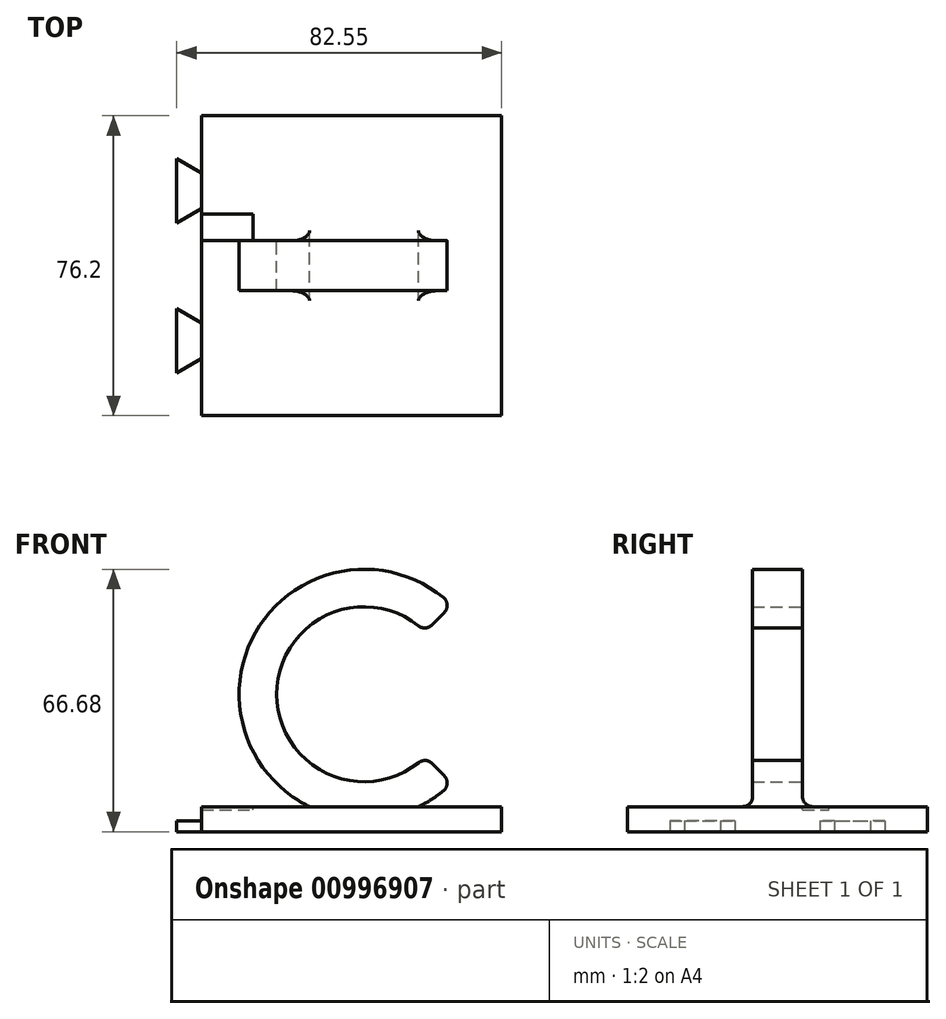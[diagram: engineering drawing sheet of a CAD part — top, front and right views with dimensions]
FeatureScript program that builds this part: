
annotation { "Feature Type Name" : "Feature", "Feature Type Description" : "" }
export const myFeature = defineFeature(function(context is Context, id is Id, definition is map)
    precondition{}
    {
        {
            var Q0;
            Q0=qCreatedBy(makeId("Top.planeOp"),FACE);
            var sketch = newSketch(context, id + "F0", { "sketchPlane" : qUnion([Q0])});
            skLineSegment(sketch, "E0.bottom", {"start": v(38.1, -38.1) * mm, "end": v(-38.1, -38.1) * mm});
            skLineSegment(sketch, "E0.top", {"start": v(38.1, 38.1) * mm, "end": v(-38.1, 38.1) * mm});
            skLineSegment(sketch, "E0.left", {"start": v(38.1, -38.1) * mm, "end": v(38.1, 38.1) * mm});
            skLineSegment(sketch, "E0.right", {"start": v(-38.1, -38.1) * mm, "end": v(-38.1, 38.1) * mm});
            skPoint(sketch, "E0.middle", {"position": v(0, 0) * mm});
            skSolve(sketch);
        }
        {
            var Q0;
            Q0=qCreatedBy(makeId("Front.planeOp"),FACE);
            var sketch = newSketch(context, id + "F1", { "sketchPlane" : qUnion([Q0])});
            skArc(sketch, "E1", {"start": v(25.4, 51.25) * mm, "mid": v(-28.58, 28.58) * mm, "end": v(25.4, 5.9) * mm});
            skLineSegment(sketch, "E2", {"start": v(16.41, 60.33) * mm, "end": v(-26.64, 60.33) * mm, "construction": true});
            skLineSegment(sketch, "E3", {"start": v(-19.56, -3.18) * mm, "end": v(26.32, -3.17) * mm, "construction": true});
            skArc(sketch, "E4", {"start": v(18.73, 44.45) * mm, "mid": v(-19.05, 28.58) * mm, "end": v(18.73, 12.7) * mm});
            skLineSegment(sketch, "E5", {"start": v(25.4, 51.25) * mm, "end": v(18.73, 44.45) * mm});
            skLineSegment(sketch, "E6", {"start": v(18.73, 12.7) * mm, "end": v(25.4, 5.9) * mm});
            skLineSegment(sketch, "E7", {"start": v(18.73, 44.45) * mm, "end": v(34.7, 28.8) * mm, "construction": true});
            skSolve(sketch);
        }
        {
            var Q0;
            Q0=qSketchRegion(id+"F0",true);
            extrude(context, id + "F2", {"entities" : qUnion([Q0]), "oppositeDirection" : true, "depth" : 6.35 * mm, "offsetDistance" : 25.4 * mm});
        }
        {
            var Q0;
            Q0=qSketchRegion(id+"F1",true);
            extrude(context, id + "F3", {"entities" : qUnion([Q0]), "operationType" : NewBodyOperationType.ADD, "endBound" : BoundingType.SYMMETRIC, "depth" : 12.7 * mm, "offsetDistance" : 25.4 * mm});
        }
        {
            var Q0;
            Q0=makeQuery(id+"F3.opExtrude","SWEPT_EDGE",EDGE,{"disambiguationData":[OSD([sQuery(id+"F1.wireOp",EDGE,"E1"),sQuery(id+"F1.wireOp",EDGE,"E5")])]});
            var Q1;
            Q1=makeQuery(id+"F3.opExtrude","SWEPT_EDGE",EDGE,{"disambiguationData":[OSD([sQuery(id+"F1.wireOp",EDGE,"E4"),sQuery(id+"F1.wireOp",EDGE,"E5")])]});
            var Q2;
            Q2=makeQuery(id+"F3.opExtrude","SWEPT_EDGE",EDGE,{"disambiguationData":[OSD([sQuery(id+"F1.wireOp",EDGE,"E4"),sQuery(id+"F1.wireOp",EDGE,"E6")])]});
            var Q3;
            Q3=makeQuery(id+"F3.opExtrude","SWEPT_EDGE",EDGE,{"disambiguationData":[OSD([sQuery(id+"F1.wireOp",EDGE,"E1"),sQuery(id+"F1.wireOp",EDGE,"E6")])]});
            var Q4;
            Q4=makeQuery(id+"F3.boolean.opBoolean","INTERSECT",EDGE,{"derivedFrom":[makeQuery(id+"F2.opExtrude","CAP_FACE",FACE,{"disambiguationData":[OSD([sQuery(id+"F0.wireOp",EDGE,"E0.bottom"),sQuery(id+"F0.wireOp",EDGE,"E0.top"),sQuery(id+"F0.wireOp",EDGE,"E0.left"),sQuery(id+"F0.wireOp",EDGE,"E0.right")])],"isStart":true}),makeQuery(id+"F3.opExtrude","CAP_FACE",FACE,{"disambiguationData":[OSD([sQuery(id+"F1.wireOp",EDGE,"E1"),sQuery(id+"F1.wireOp",EDGE,"E4"),sQuery(id+"F1.wireOp",EDGE,"E5"),sQuery(id+"F1.wireOp",EDGE,"E6")])],"isStart":false})]});
            var Q5;
            Q5=makeQuery(id+"F3.boolean.opBoolean","INTERSECT",EDGE,{"derivedFrom":[makeQuery(id+"F2.opExtrude","CAP_FACE",FACE,{"disambiguationData":[OSD([sQuery(id+"F0.wireOp",EDGE,"E0.bottom"),sQuery(id+"F0.wireOp",EDGE,"E0.top"),sQuery(id+"F0.wireOp",EDGE,"E0.left"),sQuery(id+"F0.wireOp",EDGE,"E0.right")])],"isStart":true}),makeQuery(id+"F3.opExtrude","CAP_FACE",FACE,{"disambiguationData":[OSD([sQuery(id+"F1.wireOp",EDGE,"E1"),sQuery(id+"F1.wireOp",EDGE,"E4"),sQuery(id+"F1.wireOp",EDGE,"E5"),sQuery(id+"F1.wireOp",EDGE,"E6")])],"isStart":true})]});
            fillet(context, id + "F4", {"entities" : qUnion([Q0, Q1, Q2, Q3, Q4, Q5]), "radius" : 2.54 * mm, "tangentPropagation" : true, "allowEdgeOverflow" : false});
        }
        {
            var Q0;
            Q0=makeQuery(id+"F2.opExtrude","CAP_FACE",FACE,{"disambiguationData":[OSD([sQuery(id+"F0.wireOp",EDGE,"E0.bottom"),sQuery(id+"F0.wireOp",EDGE,"E0.top"),sQuery(id+"F0.wireOp",EDGE,"E0.left"),sQuery(id+"F0.wireOp",EDGE,"E0.right")])],"isStart":false});
            var sketch = newSketch(context, id + "F5", { "sketchPlane" : qUnion([Q0])});
            skLineSegment(sketch, "E8", {"start": v(-38.1, 23.61) * mm, "end": v(-38.1, 14.49) * mm});
            skLineSegment(sketch, "E9", {"start": v(-38.1, 14.49) * mm, "end": v(-44.45, 10.82) * mm});
            skLineSegment(sketch, "E10", {"start": v(-44.45, 10.82) * mm, "end": v(-44.45, 27.28) * mm});
            skLineSegment(sketch, "E11", {"start": v(-44.45, 27.28) * mm, "end": v(-38.1, 23.61) * mm});
            skLineSegment(sketch, "E12", {"start": v(-38.1, 19.05) * mm, "end": v(-38.1, 38.1) * mm, "construction": true});
            skLineSegment(sketch, "E13.MirrorCS", {"start": v(-38.1, -14.49) * mm, "end": v(-44.45, -10.82) * mm});
            skLineSegment(sketch, "E14.MirrorCS", {"start": v(-44.45, -10.82) * mm, "end": v(-44.45, -27.28) * mm});
            skLineSegment(sketch, "E15.MirrorCS", {"start": v(-38.1, -23.61) * mm, "end": v(-38.1, -14.49) * mm});
            skLineSegment(sketch, "E16.MirrorCS", {"start": v(-44.45, -27.28) * mm, "end": v(-38.1, -23.61) * mm});
            skSolve(sketch);
        }
        {
            var Q0;
            Q0=qSketchRegion(id+"F5",true);
            extrude(context, id + "F6", {"entities" : qUnion([Q0]), "operationType" : NewBodyOperationType.ADD, "oppositeDirection" : true, "depth" : 2.78 * mm, "offsetDistance" : 25.4 * mm});
        }
        {
            var Q0;
            Q0=makeQuery(id+"F2.opExtrude","CAP_FACE",FACE,{"disambiguationData":[OSD([sQuery(id+"F0.wireOp",EDGE,"E0.bottom"),sQuery(id+"F0.wireOp",EDGE,"E0.top"),sQuery(id+"F0.wireOp",EDGE,"E0.left"),sQuery(id+"F0.wireOp",EDGE,"E0.right")])],"isStart":true});
            var sketch = newSketch(context, id + "F7", { "sketchPlane" : qUnion([Q0])});
            skLineSegment(sketch, "E17", {"start": v(-38.1, 6.35) * mm, "end": v(38.1, 6.35) * mm, "construction": true});
            skLineSegment(sketch, "E18.bottom", {"start": v(-38.1, 6.35) * mm, "end": v(-25, 6.35) * mm});
            skLineSegment(sketch, "E18.top", {"start": v(-38.1, 13.1) * mm, "end": v(-25, 13.1) * mm});
            skLineSegment(sketch, "E18.left", {"start": v(-38.1, 6.35) * mm, "end": v(-38.1, 13.1) * mm});
            skLineSegment(sketch, "E18.right", {"start": v(-25, 6.35) * mm, "end": v(-25, 13.1) * mm});
            skSolve(sketch);
        }
        {
            var Q0;
            Q0 = qSketchRegion(id + "F7", true);
            extrude(context, id + "F8", {"entities" : qUnion([Q0]), "operationType" : NewBodyOperationType.REMOVE, "oppositeDirection" : true, "depth" : 0.8 * mm, "offsetDistance" : 25.4 * mm});
        }
    });
